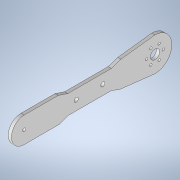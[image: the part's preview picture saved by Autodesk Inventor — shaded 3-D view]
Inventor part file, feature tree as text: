
AUTODESK INVENTOR PART (.ipt)
format: ipt  version: 2022 (Build 260153000, 153)  size: 148,992 bytes
history: native  units: mm
features: extrude x1, sketch x1
ambient origin geometry x8: Origin, YZ Plane, XZ Plane, XY Plane, X Axis, Y Axis, Z Axis, Center Point
bodies: Solid1 (feature_tree)
feature tree (2):
  extrude  "Extrusion1"  Depth=3.0mm
  sketch  "Sketch1"  dims[d1=60.0mm d3=8.75mm d4=18.0mm d5=1.2mm d6=4.0mm d7=360.0deg d8=45.0mm d9=8.0mm d10=9.0mm d11=9.0mm d13=8.0mm d14=12.5mm d15=3.0mm d16=3.0mm d17=0.0mm d19=24.0mm]
